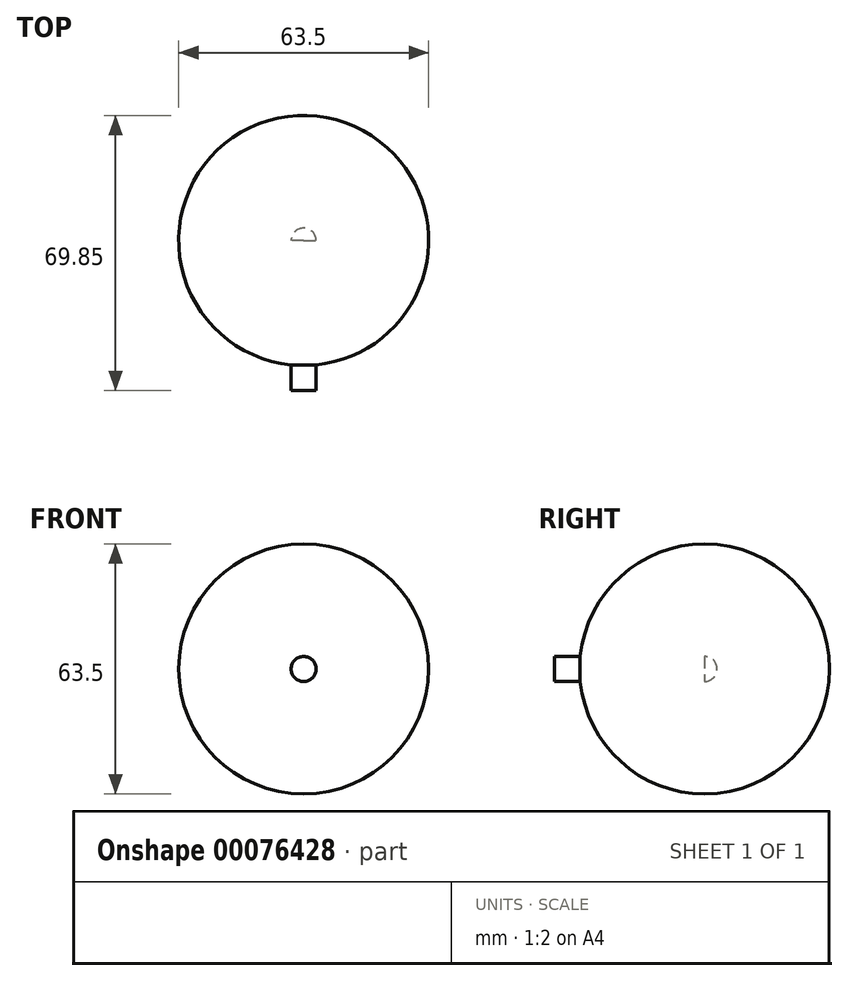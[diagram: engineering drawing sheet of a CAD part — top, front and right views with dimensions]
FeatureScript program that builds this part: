
annotation { "Feature Type Name" : "Feature", "Feature Type Description" : "" }
export const myFeature = defineFeature(function(context is Context, id is Id, definition is map)
    precondition{}
    {
        {
            var Q0;
            Q0=qCreatedBy(makeId("Front.planeOp"),FACE);
            var sketch = newSketch(context, id + "F0", { "sketchPlane" : qUnion([Q0])});
            skLineSegment(sketch, "E0.bottom", {"start": v(-101.6, 101.6) * mm, "end": v(101.6, 101.6) * mm, "construction": true});
            skLineSegment(sketch, "E0.top", {"start": v(-101.6, -101.6) * mm, "end": v(101.6, -101.6) * mm, "construction": true});
            skLineSegment(sketch, "E0.left", {"start": v(-101.6, 101.6) * mm, "end": v(-101.6, -101.6) * mm, "construction": true});
            skLineSegment(sketch, "E0.right", {"start": v(101.6, 101.6) * mm, "end": v(101.6, -101.6) * mm, "construction": true});
            skArc(sketch, "E1", {"start": v(0, -31.75) * mm, "mid": v(31.75, 0) * mm, "end": v(0, 31.75) * mm});
            skLineSegment(sketch, "E2", {"start": v(0, 31.75) * mm, "end": v(0, -31.75) * mm});
            skCircle(sketch, "E3", {"center": v(0, 0) * mm, "radius": 3.18 * mm});
            skSolve(sketch);
        }
        {
            var Q0;
            Q0=makeQuery(id+"F0.imprint","IMPRINT",FACE,{"disambiguationData":[TD([[makeQuery(id+"F0.imprint","IMPRINT",EDGE,{"derivedFrom":sQuery(id+"F0.wireOp",EDGE,"E1")}),1.0]])]});
            var Q1;
            Q1=sQuery(id+"F0.wireOp",EDGE,"E2");
            revolve(context, id + "F1", {"entities" : qUnion([Q0]), "axis" : qUnion([Q1]), "revolveType" : RevolveType.FULL});
        }
        {
            var Q0;
            {var subQ0=sQuery(id+"F0.wireOp",EDGE,"E3");var subQ1=sQuery(id+"F0.wireOp",EDGE,"E2");var subQ2=makeQuery(id+"F0.imprint","INTERSECT",VERTEX,{"disambiguationData":[OD(0.0)],"derivedFrom":[subQ1,subQ0]});Q0=makeQuery(id+"F0.imprint","IMPRINT",FACE,{"disambiguationData":[TD([[makeQuery(id+"F0.imprint","IMPRINT",EDGE,{"disambiguationData":[TD([[subQ2,-1.0]])],"derivedFrom":subQ1}),-1.0]])]});}
            var Q1;
            {var subQ0=sQuery(id+"F0.wireOp",EDGE,"E3");var subQ1=sQuery(id+"F0.wireOp",EDGE,"E2");var subQ2=makeQuery(id+"F0.imprint","INTERSECT",VERTEX,{"disambiguationData":[OD(0.0)],"derivedFrom":[subQ1,subQ0]});Q1=makeQuery(id+"F0.imprint","IMPRINT",FACE,{"disambiguationData":[TD([[makeQuery(id+"F0.imprint","IMPRINT",EDGE,{"disambiguationData":[TD([[subQ2,-1.0]])],"derivedFrom":subQ1}),1.0]])]});}
            extrude(context, id + "F2", {"entities" : qUnion([Q0, Q1]), "operationType" : NewBodyOperationType.ADD, "depth" : 38.1 * mm});
        }
    });
